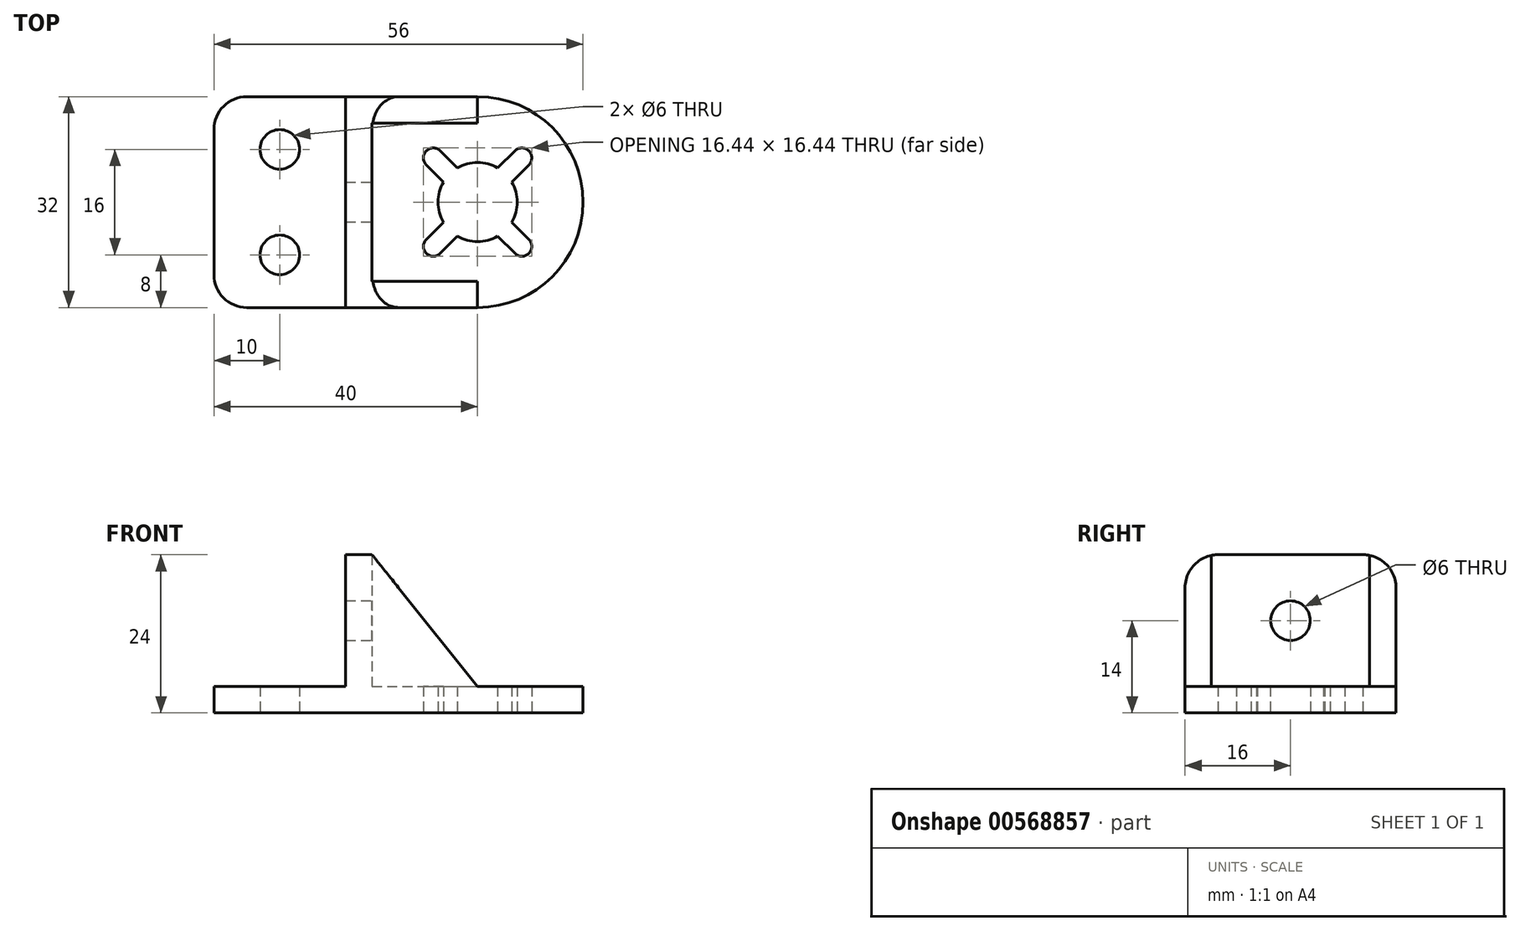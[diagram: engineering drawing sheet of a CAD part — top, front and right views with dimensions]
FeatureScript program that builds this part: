
annotation { "Feature Type Name" : "Feature", "Feature Type Description" : "" }
export const myFeature = defineFeature(function(context is Context, id is Id, definition is map)
    precondition{}
    {
        {
            var Q0;
            Q0=qCreatedBy(makeId("Top.planeOp"),FACE);
            var sketch = newSketch(context, id + "F0", { "sketchPlane" : qUnion([Q0])});
            skLineSegment(sketch, "E0", {"start": v(0, 96.3) * mm, "end": v(0, 0) * mm, "construction": true});
            skLineSegment(sketch, "E1", {"start": v(-20, 0) * mm, "end": v(-20, 94.97) * mm, "construction": true});
            skLineSegment(sketch, "E2", {"start": v(-84.45, 0) * mm, "end": v(85.66, 0) * mm, "construction": true});
            skCircle(sketch, "E3", {"center": v(20, 21) * mm, "radius": 4 * mm, "construction": true});
            skCircle(sketch, "E4", {"center": v(20, 21) * mm, "radius": 5 * mm, "construction": true});
            skCircle(sketch, "E5", {"center": v(20, 21) * mm, "radius": 6 * mm});
            skCircle(sketch, "E6", {"center": v(20, 21) * mm, "radius": 16 * mm});
            skLineSegment(sketch, "E7", {"start": v(0, 5) * mm, "end": v(4, 5) * mm});
            skLineSegment(sketch, "E8", {"start": v(4, 37) * mm, "end": v(20, 37) * mm});
            skLineSegment(sketch, "E9", {"start": v(4, 37) * mm, "end": v(0, 37) * mm});
            skLineSegment(sketch, "E10", {"start": v(4, 37) * mm, "end": v(4, 5) * mm});
            skLineSegment(sketch, "E11", {"start": v(0, 37) * mm, "end": v(0, 5) * mm});
            skLineSegment(sketch, "E12", {"start": v(0, 37) * mm, "end": v(-20, 37) * mm});
            skLineSegment(sketch, "E13", {"start": v(-20, 37) * mm, "end": v(-20, 5) * mm});
            skLineSegment(sketch, "E14", {"start": v(-20, 5) * mm, "end": v(0, 5) * mm});
            skArc(sketch, "E15", {"start": v(25.66, 13.22) * mm, "mid": v(27.78, 13.22) * mm, "end": v(27.78, 15.34) * mm});
            skLineSegment(sketch, "E16", {"start": v(23.05, 15.83) * mm, "end": v(25.66, 13.22) * mm});
            skLineSegment(sketch, "E17", {"start": v(27.78, 15.34) * mm, "end": v(25.17, 17.95) * mm});
            skLineSegment(sketch, "E18", {"start": v(20, 21) * mm, "end": v(26.72, 14.28) * mm, "construction": true});
            skLineSegment(sketch, "E19.1.0", {"start": v(25.66, 28.78) * mm, "end": v(23.05, 26.17) * mm});
            skArc(sketch, "E19.1.1", {"start": v(27.78, 26.66) * mm, "mid": v(27.78, 28.78) * mm, "end": v(25.66, 28.78) * mm});
            skLineSegment(sketch, "E19.1.2", {"start": v(25.17, 24.05) * mm, "end": v(27.78, 26.66) * mm});
            skLineSegment(sketch, "E19.1.3", {"start": v(20, 21) * mm, "end": v(26.72, 27.72) * mm, "construction": true});
            skLineSegment(sketch, "E19.2.0", {"start": v(12.22, 26.66) * mm, "end": v(14.83, 24.05) * mm});
            skArc(sketch, "E19.2.1", {"start": v(14.34, 28.78) * mm, "mid": v(12.22, 28.78) * mm, "end": v(12.22, 26.66) * mm});
            skLineSegment(sketch, "E19.2.2", {"start": v(16.95, 26.17) * mm, "end": v(14.34, 28.78) * mm});
            skLineSegment(sketch, "E19.2.3", {"start": v(20, 21) * mm, "end": v(13.28, 27.72) * mm, "construction": true});
            skLineSegment(sketch, "E19.3.0", {"start": v(14.34, 13.22) * mm, "end": v(16.95, 15.83) * mm});
            skArc(sketch, "E19.3.1", {"start": v(12.22, 15.34) * mm, "mid": v(12.22, 13.22) * mm, "end": v(14.34, 13.22) * mm});
            skLineSegment(sketch, "E19.3.2", {"start": v(14.83, 17.95) * mm, "end": v(12.22, 15.34) * mm});
            skLineSegment(sketch, "E19.3.3", {"start": v(20, 21) * mm, "end": v(13.28, 14.28) * mm, "construction": true});
            skLineSegment(sketch, "E20", {"start": v(39.84, 21) * mm, "end": v(20, 21) * mm, "construction": true});
            skCircle(sketch, "E21", {"center": v(-10, 29) * mm, "radius": 3 * mm});
            skCircle(sketch, "E22", {"center": v(-10, 13) * mm, "radius": 3 * mm});
            skLineSegment(sketch, "E23", {"start": v(-10, 37) * mm, "end": v(-10, 5) * mm, "construction": true});
            skLineSegment(sketch, "E24", {"start": v(4, 5) * mm, "end": v(20, 5) * mm});
            skSolve(sketch);
        }
        {
            var Q0;
            Q0 = qSketchRegion(id + "F0", true);
            extrude(context, id + "F1", {"entities" : qUnion([Q0]), "depth" : 4 * mm, "offsetDistance" : 25 * mm});
        }
        {
            var Q0;
            Q0=makeQuery(id+"F0.imprint","IMPRINT",FACE,{"disambiguationData":[TD([[makeQuery(id+"F0.imprint","IMPRINT",EDGE,{"derivedFrom":sQuery(id+"F0.wireOp",EDGE,"E9")}),1.0]])]});
            extrude(context, id + "F2", {"entities" : qUnion([Q0]), "operationType" : NewBodyOperationType.ADD, "depth" : 24 * mm, "offsetDistance" : 25 * mm});
        }
        {
            var Q0;
            {var subQ0=sQuery(id+"F0.wireOp",EDGE,"E19.3.2");var subQ1=sQuery(id+"F0.wireOp",EDGE,"E19.3.1");var subQ2=sQuery(id+"F0.wireOp",EDGE,"E19.3.0");var subQ3=sQuery(id+"F0.wireOp",EDGE,"E19.2.2");var subQ4=sQuery(id+"F0.wireOp",EDGE,"E19.2.1");var subQ5=sQuery(id+"F0.wireOp",EDGE,"E19.2.0");var subQ6=sQuery(id+"F0.wireOp",EDGE,"E19.1.2");var subQ7=sQuery(id+"F0.wireOp",EDGE,"E19.1.1");var subQ8=sQuery(id+"F0.wireOp",EDGE,"E19.1.0");var subQ9=sQuery(id+"F0.wireOp",EDGE,"E17");var subQ10=sQuery(id+"F0.wireOp",EDGE,"E16");var subQ11=sQuery(id+"F0.wireOp",EDGE,"E5");var subQ12=sQuery(id+"F0.wireOp",EDGE,"E15");var subQ13=sQuery(id+"F0.wireOp",EDGE,"E6");var subQ14=sQuery(id+"F0.wireOp",EDGE,"E14");var subQ15=sQuery(id+"F0.wireOp",EDGE,"E7");var subQ16=sQuery(id+"F0.wireOp",EDGE,"E8");var subQ17=sQuery(id+"F0.wireOp",EDGE,"E12");var subQ18=sQuery(id+"F0.wireOp",EDGE,"E9");Q0=makeQuery(id+"F2.boolean.opBoolean","SPLIT",FACE,{"disambiguationData":[TD([makeQuery(id+"F1.opExtrude","SWEPT_FACE",FACE,{"disambiguationData":[OSD([subQ13])]})])],"derivedFrom":makeQuery(id+"F1.opExtrude","CAP_FACE",FACE,{"disambiguationData":[OSD([subQ11,subQ13,subQ15,subQ16,subQ18,subQ17,sQuery(id+"F0.wireOp",EDGE,"E13"),subQ14,subQ12,subQ10,subQ9,subQ8,subQ7,subQ6,subQ5,subQ4,subQ3,subQ2,subQ1,subQ0,sQuery(id+"F0.wireOp",EDGE,"E21"),sQuery(id+"F0.wireOp",EDGE,"E22")])],"isStart":false})});}
            var sketch = newSketch(context, id + "F3", { "sketchPlane" : qUnion([Q0])});
            skArc(sketch, "E25.1", {"start": v(20, 5) * mm, "mid": v(36, 21) * mm, "end": v(20, 37) * mm, "construction": true});
            skLineSegment(sketch, "E25.2", {"start": v(4, 5) * mm, "end": v(4, 37) * mm, "construction": true});
            skLineSegment(sketch, "E25.3", {"start": v(4, 37) * mm, "end": v(20, 37) * mm, "construction": true});
            skLineSegment(sketch, "E26.0", {"start": v(14.34, 13.22) * mm, "end": v(16.95, 15.83) * mm, "construction": true});
            skArc(sketch, "E26.1", {"start": v(12.22, 15.34) * mm, "mid": v(12.22, 13.22) * mm, "end": v(14.34, 13.22) * mm, "construction": true});
            skArc(sketch, "E26.2", {"start": v(16.95, 15.83) * mm, "mid": v(20, 15) * mm, "end": v(23.05, 15.83) * mm, "construction": true});
            skLineSegment(sketch, "E26.3", {"start": v(23.05, 15.83) * mm, "end": v(25.66, 13.22) * mm, "construction": true});
            skArc(sketch, "E26.4", {"start": v(25.66, 13.22) * mm, "mid": v(27.78, 13.22) * mm, "end": v(27.78, 15.34) * mm, "construction": true});
            skLineSegment(sketch, "E26.5", {"start": v(27.78, 15.34) * mm, "end": v(25.17, 17.95) * mm, "construction": true});
            skLineSegment(sketch, "E27.bottom", {"start": v(4, 5) * mm, "end": v(20, 5) * mm});
            skLineSegment(sketch, "E27.top", {"start": v(4, 9) * mm, "end": v(20, 9) * mm});
            skLineSegment(sketch, "E27.left", {"start": v(4, 5) * mm, "end": v(4, 9) * mm});
            skLineSegment(sketch, "E27.right", {"start": v(20, 5) * mm, "end": v(20, 9) * mm});
            skLineSegment(sketch, "E28.bottom", {"start": v(4, 37) * mm, "end": v(20, 37) * mm});
            skLineSegment(sketch, "E28.top", {"start": v(4, 33) * mm, "end": v(20, 33) * mm});
            skLineSegment(sketch, "E28.left", {"start": v(4, 37) * mm, "end": v(4, 33) * mm});
            skLineSegment(sketch, "E28.right", {"start": v(20, 37) * mm, "end": v(20, 33) * mm});
            skSolve(sketch);
        }
        {
            var Q0;
            Q0 = qSketchRegion(id + "F3", true);
            extrude(context, id + "F4", {"entities" : qUnion([Q0]), "operationType" : NewBodyOperationType.ADD, "depth" : 20 * mm, "offsetDistance" : 25 * mm});
        }
        {
            var Q0;
            Q0=makeQuery(id+"F4.opExtrude","CAP_EDGE",EDGE,{"disambiguationData":[OSD([sQuery(id+"F3.wireOp",EDGE,"E27.right")])],"isStart":false});
            var Q1;
            Q1=makeQuery(id+"F4.opExtrude","CAP_EDGE",EDGE,{"disambiguationData":[OSD([sQuery(id+"F3.wireOp",EDGE,"E28.right")])],"isStart":false});
            chamfer(context, id + "F5", {"entities" : qUnion([Q0, Q1]), "chamferType" : ChamferType.TWO_OFFSETS, "width1" : 16 * mm, "oppositeDirection" : false, "width2" : 20 * mm, "tangentPropagation" : true});
        }
        {
            var Q0;
            Q0=makeQuery(id+"F2.opExtrude","SWEPT_FACE",FACE,{"disambiguationData":[OSD([sQuery(id+"F0.wireOp",EDGE,"E10")])]});
            var sketch = newSketch(context, id + "F6", { "sketchPlane" : qUnion([Q0])});
            skLineSegment(sketch, "E29", {"start": v(9, 14) * mm, "end": v(33, 14) * mm, "construction": true});
            skCircle(sketch, "E30", {"center": v(21, 14) * mm, "radius": 3 * mm});
            skSolve(sketch);
        }
        {
            var Q0;
            Q0 = qSketchRegion(id + "F6", true);
            extrude(context, id + "F7", {"entities" : qUnion([Q0]), "operationType" : NewBodyOperationType.REMOVE, "oppositeDirection" : true, "depth" : 25 * mm, "offsetDistance" : 25 * mm});
        }
        {
            var Q0;
            Q0=makeQuery(id+"F1.opExtrude","SWEPT_EDGE",EDGE,{"disambiguationData":[OSD([sQuery(id+"F0.wireOp",EDGE,"E13"),sQuery(id+"F0.wireOp",EDGE,"E14")])]});
            var Q1;
            Q1=makeQuery(id+"F2.opExtrude","CAP_EDGE",EDGE,{"disambiguationData":[OSD([sQuery(id+"F0.wireOp",EDGE,"E7")])],"isStart":false});
            var Q2;
            Q2=makeQuery(id+"F2.opExtrude","CAP_EDGE",EDGE,{"disambiguationData":[OSD([sQuery(id+"F0.wireOp",EDGE,"E9")])],"isStart":false});
            var Q3;
            Q3=makeQuery(id+"F1.opExtrude","SWEPT_EDGE",EDGE,{"disambiguationData":[OSD([sQuery(id+"F0.wireOp",EDGE,"E12"),sQuery(id+"F0.wireOp",EDGE,"E13")])]});
            fillet(context, id + "F8", {"entities" : qUnion([Q0, Q1, Q2, Q3]), "radius" : 5 * mm, "tangentPropagation" : true, "allowEdgeOverflow" : false});
        }
    });
